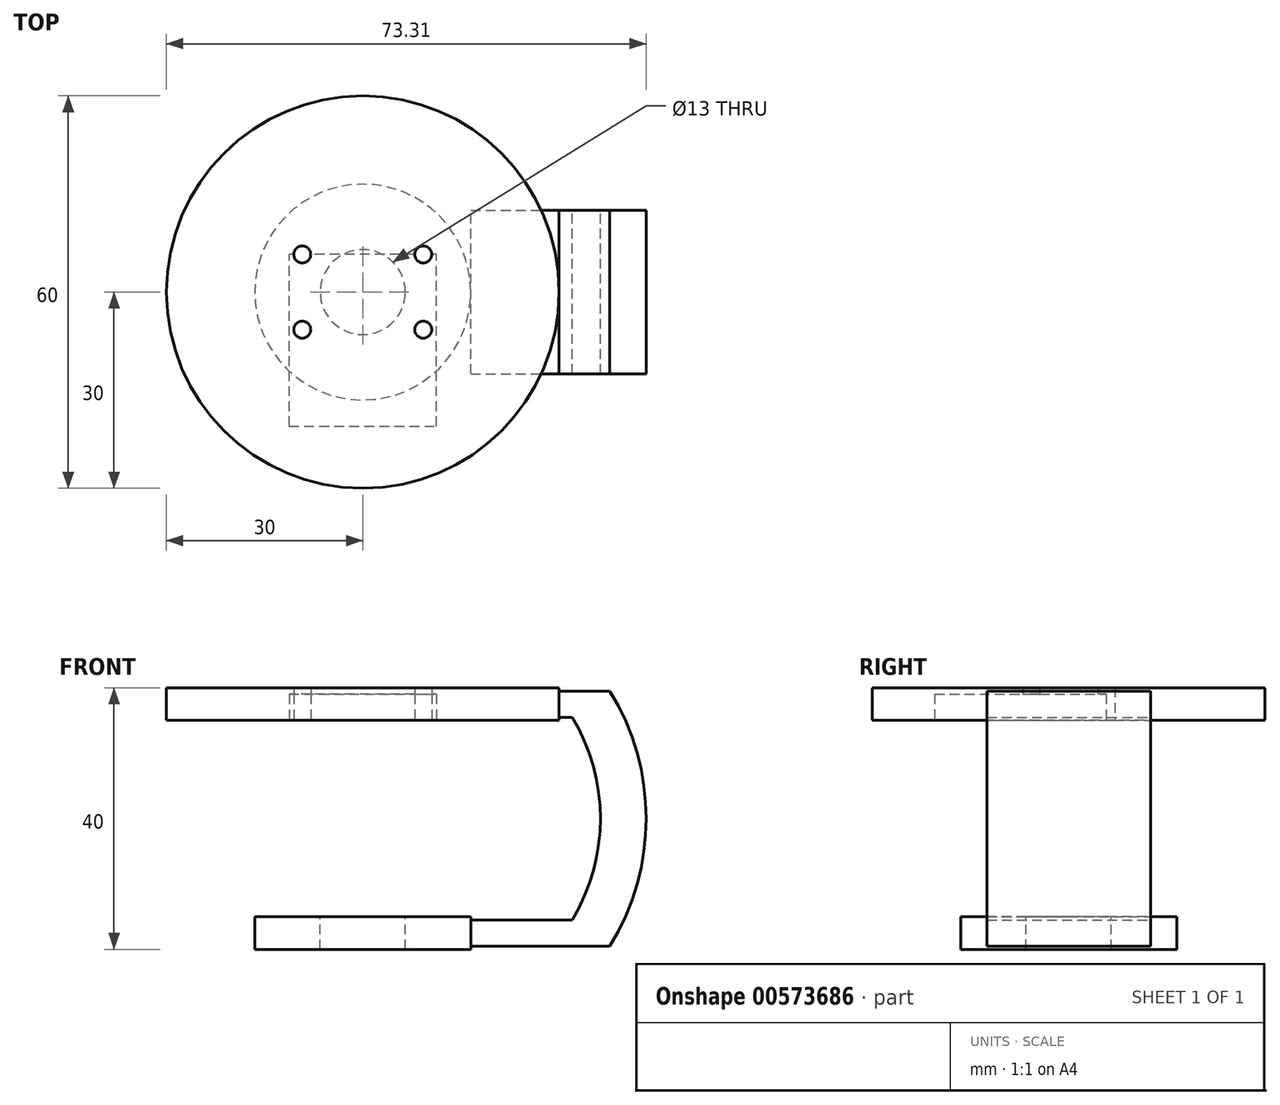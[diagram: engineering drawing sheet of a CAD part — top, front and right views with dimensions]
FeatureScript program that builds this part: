
annotation { "Feature Type Name" : "Feature", "Feature Type Description" : "" }
export const myFeature = defineFeature(function(context is Context, id is Id, definition is map)
    precondition{}
    {
        {
            var Q0;
            Q0=qCreatedBy(makeId("Front.planeOp"),FACE);
            var sketch = newSketch(context, id + "F0", { "sketchPlane" : qUnion([Q0])});
            skLineSegment(sketch, "E0.bottom", {"start": v(16.5, 2.5) * mm, "end": v(-16.5, 2.5) * mm});
            skLineSegment(sketch, "E0.top", {"start": v(16.5, -2.5) * mm, "end": v(-16.5, -2.5) * mm});
            skLineSegment(sketch, "E0.left", {"start": v(16.5, 2.5) * mm, "end": v(16.5, -2.5) * mm});
            skLineSegment(sketch, "E0.right", {"start": v(-16.5, 2.5) * mm, "end": v(-16.5, -2.5) * mm});
            skPoint(sketch, "E0.middle", {"position": v(0, 0) * mm});
            skLineSegment(sketch, "E1", {"start": v(0, 2.5) * mm, "end": v(0, -2.5) * mm});
            skLineSegment(sketch, "E2.bottom", {"start": v(0, -2) * mm, "end": v(32, -2) * mm});
            skLineSegment(sketch, "E2.top", {"start": v(0, 2) * mm, "end": v(32, 2) * mm});
            skLineSegment(sketch, "E2.left", {"start": v(0, -2) * mm, "end": v(0, 2) * mm});
            skLineSegment(sketch, "E2.right", {"start": v(32, -2) * mm, "end": v(32, 2) * mm});
            skLineSegment(sketch, "E3.bottom", {"start": v(30, 37.5) * mm, "end": v(-30, 37.5) * mm});
            skLineSegment(sketch, "E3.top", {"start": v(30, 32.5) * mm, "end": v(-30, 32.5) * mm});
            skLineSegment(sketch, "E3.left", {"start": v(30, 37.5) * mm, "end": v(30, 32.5) * mm});
            skLineSegment(sketch, "E3.right", {"start": v(-30, 37.5) * mm, "end": v(-30, 32.5) * mm});
            skPoint(sketch, "E3.middle", {"position": v(0, 35) * mm});
            skLineSegment(sketch, "E4", {"start": v(0, 37.5) * mm, "end": v(0, 32.5) * mm});
            skLineSegment(sketch, "E5.bottom", {"start": v(0, 33) * mm, "end": v(32, 33) * mm});
            skLineSegment(sketch, "E5.top", {"start": v(0, 37) * mm, "end": v(32, 37) * mm});
            skLineSegment(sketch, "E5.left", {"start": v(0, 33) * mm, "end": v(0, 37) * mm});
            skLineSegment(sketch, "E5.right", {"start": v(32, 33) * mm, "end": v(32, 37) * mm});
            skArc(sketch, "E6", {"start": v(32, 2) * mm, "mid": v(36.31, 17.5) * mm, "end": v(32, 33) * mm});
            skArc(sketch, "E7.0", {"start": v(37.76, -2) * mm, "mid": v(43.31, 17.5) * mm, "end": v(37.76, 37) * mm});
            skLineSegment(sketch, "E8", {"start": v(32, 37) * mm, "end": v(37.76, 37) * mm});
            skLineSegment(sketch, "E9", {"start": v(32, -2) * mm, "end": v(37.76, -2) * mm});
            skSolve(sketch);
        }
        {
            var Q0;
            {var subQ0=sQuery(id+"F0.wireOp",EDGE,"E0.right");Q0=makeQuery(id+"F0.imprint","IMPRINT",FACE,{"disambiguationData":[TD([[makeQuery(id+"F0.imprint","IMPRINT",EDGE,{"derivedFrom":subQ0}),1.0]])]});}
            var Q1;
            Q1=sQuery(id+"F0.wireOp",EDGE,"E1");
            revolve(context, id + "F1", {"entities" : qUnion([Q0]), "axis" : qUnion([Q1]), "revolveType" : RevolveType.FULL});
        }
        {
            var Q0;
            {var subQ0=sQuery(id+"F0.wireOp",EDGE,"E3.right");Q0=makeQuery(id+"F0.imprint","IMPRINT",FACE,{"disambiguationData":[TD([[makeQuery(id+"F0.imprint","IMPRINT",EDGE,{"derivedFrom":subQ0}),1.0]])]});}
            var Q1;
            Q1=sQuery(id+"F0.wireOp",EDGE,"E4");
            revolve(context, id + "F2", {"entities" : qUnion([Q0]), "axis" : qUnion([Q1]), "revolveType" : RevolveType.FULL});
        }
        {
            var Q0;
            {var subQ5=sQuery(id+"F0.wireOp",EDGE,"E2.right");Q0=makeQuery(id+"F0.imprint","IMPRINT",FACE,{"disambiguationData":[TD([[makeQuery(id+"F0.imprint","IMPRINT",EDGE,{"derivedFrom":subQ5}),1.0]])]});}
            var Q1;
            Q1=makeQuery(id+"F0.imprint","IMPRINT",FACE,{"disambiguationData":[TD([[makeQuery(id+"F0.imprint","IMPRINT",EDGE,{"derivedFrom":sQuery(id+"F0.wireOp",EDGE,"E2.right")}),-1.0]])]});
            var Q2;
            {var subQ5=sQuery(id+"F0.wireOp",EDGE,"E5.right");Q2=makeQuery(id+"F0.imprint","IMPRINT",FACE,{"disambiguationData":[TD([[makeQuery(id+"F0.imprint","IMPRINT",EDGE,{"derivedFrom":subQ5}),1.0]])]});}
            var Q3;
            {var subQ5=sQuery(id+"F0.wireOp",EDGE,"E2.left");Q3=makeQuery(id+"F0.imprint","IMPRINT",FACE,{"disambiguationData":[TD([[makeQuery(id+"F0.imprint","IMPRINT",EDGE,{"derivedFrom":subQ5}),-1.0]])]});}
            var Q4;
            {var subQ5=sQuery(id+"F0.wireOp",EDGE,"E5.left");Q4=makeQuery(id+"F0.imprint","IMPRINT",FACE,{"disambiguationData":[TD([[makeQuery(id+"F0.imprint","IMPRINT",EDGE,{"derivedFrom":subQ5}),-1.0]])]});}
            extrude(context, id + "F3", {"entities" : qUnion([Q0, Q1, Q2, Q3, Q4]), "endBound" : BoundingType.SYMMETRIC, "depth" : 25 * mm, "offsetDistance" : 25 * mm});
        }
        {
            var Q0;
            Q0=makeQuery(id+"F1.opRevolve","SWEPT_FACE",FACE,{"disambiguationData":[OSD([sQuery(id+"F0.wireOp",EDGE,"E0.bottom")])]});
            var sketch = newSketch(context, id + "F4", { "sketchPlane" : qUnion([Q0])});
            skCircle(sketch, "E10", {"center": v(0, 0) * mm, "radius": 12 * mm});
            skPoint(sketch, "E11", {"position": v(0, 12) * mm});
            skSolve(sketch);
        }
        {
            var Q0;
            Q0=sQuery(id+"F4.wireOp",VERTEX,"E11");
            var Q1;
            Q1=makeQuery(id+"F2.opRevolve","SWEPT_BODY",BODY,{"disambiguationData":[OSD([sQuery(id+"F0.wireOp",EDGE,"E3.bottom"),sQuery(id+"F0.wireOp",EDGE,"E3.top"),sQuery(id+"F0.wireOp",EDGE,"E3.right"),sQuery(id+"F0.wireOp",EDGE,"E4"),sQuery(id+"F0.wireOp",EDGE,"E5.left")])]});
            hole(context, id + "F5", {"style" : HoleStyle.SIMPLE, "endStyle" : HoleEndStyle.THROUGH, "standardTappedOrClearance" : lookupTablePath({ "standard" : "ISO", "fit" : "Normal", "size" : "M3", "type" : "Clearance" }), "standardBlindInLast" : lookupTablePath({ "fit" : "Standard", "standard" : "ISO", "size" : "M3", "type" : "Clearance" }), "holeDiameter" : 3.3 * mm, "isTappedThrough" : true, "tappedDepth" : 12.7 * mm, "tapClearance" : 3, "locations" : qUnion([Q0]), "scope" : qUnion([Q1])});
        }
        {
            var Q0;
            Q0=makeQuery(id+"F1.opRevolve","SWEPT_FACE",FACE,{"disambiguationData":[OSD([sQuery(id+"F0.wireOp",EDGE,"E0.bottom")])]});
            var sketch = newSketch(context, id + "F6", { "sketchPlane" : qUnion([Q0])});
            skCircle(sketch, "E12", {"center": v(0, 0) * mm, "radius": 6.5 * mm});
            skSolve(sketch);
        }
        {
            var Q0;
            Q0=makeQuery(id+"F6.imprint","IMPRINT",FACE,{"disambiguationData":[TD([[makeQuery(id+"F6.imprint","IMPRINT",EDGE,{"derivedFrom":sQuery(id+"F6.wireOp",EDGE,"E12")}),1.0]])]});
            extrude(context, id + "F7", {"entities" : qUnion([Q0]), "operationType" : NewBodyOperationType.REMOVE, "oppositeDirection" : true, "depth" : 6 * mm, "offsetDistance" : 25 * mm});
        }
        {
            var Q0;
            Q0=makeQuery(id+"F2.opRevolve","SWEPT_FACE",FACE,{"disambiguationData":[OSD([sQuery(id+"F0.wireOp",EDGE,"E3.top")])]});
            var sketch = newSketch(context, id + "F8", { "sketchPlane" : qUnion([Q0])});
            skLineSegment(sketch, "E13.bottom", {"start": v(11.25, 5.75) * mm, "end": v(-11.25, 5.75) * mm});
            skLineSegment(sketch, "E13.top", {"start": v(11.25, -5.75) * mm, "end": v(-11.25, -5.75) * mm});
            skLineSegment(sketch, "E13.left", {"start": v(11.25, 5.75) * mm, "end": v(11.25, -5.75) * mm});
            skLineSegment(sketch, "E13.right", {"start": v(-11.25, 5.75) * mm, "end": v(-11.25, -5.75) * mm});
            skPoint(sketch, "E13.middle", {"position": v(0, 0) * mm});
            skLineSegment(sketch, "E14.bottom", {"start": v(-11.25, -5.75) * mm, "end": v(10.8, -5.75) * mm});
            skLineSegment(sketch, "E14.top", {"start": v(-11.25, 20.5) * mm, "end": v(11.25, 20.5) * mm});
            skLineSegment(sketch, "E14.left", {"start": v(-11.25, -8) * mm, "end": v(-11.25, 20.5) * mm});
            skLineSegment(sketch, "E14.right", {"start": v(11.25, -8) * mm, "end": v(11.25, 20.5) * mm});
            skLineSegment(sketch, "E15", {"start": v(-11.25, -8) * mm, "end": v(11.25, -8) * mm});
            skPoint(sketch, "E16", {"position": v(-9.25, -5.75) * mm});
            skPoint(sketch, "E17", {"position": v(9.25, -5.75) * mm});
            skPoint(sketch, "E18", {"position": v(9.25, 5.75) * mm});
            skPoint(sketch, "E19", {"position": v(-9.25, 5.75) * mm});
            skSolve(sketch);
        }
        {
            var Q0;
            Q0=sQuery(id+"F8.wireOp",VERTEX,"E16");
            var Q1;
            Q1=sQuery(id+"F8.wireOp",VERTEX,"E19");
            var Q2;
            Q2=sQuery(id+"F8.wireOp",VERTEX,"E18");
            var Q3;
            Q3=sQuery(id+"F8.wireOp",VERTEX,"E17");
            var Q4;
            Q4=makeQuery(id+"F2.opRevolve","SWEPT_BODY",BODY,{"disambiguationData":[OSD([sQuery(id+"F0.wireOp",EDGE,"E3.bottom"),sQuery(id+"F0.wireOp",EDGE,"E3.top"),sQuery(id+"F0.wireOp",EDGE,"E3.right"),sQuery(id+"F0.wireOp",EDGE,"E4"),sQuery(id+"F0.wireOp",EDGE,"E5.left")])]});
            hole(context, id + "F9", {"style" : HoleStyle.SIMPLE, "endStyle" : HoleEndStyle.THROUGH, "holeDiameter" : 2.6 * mm, "isTappedThrough" : true, "tappedDepth" : 12.7 * mm, "tapClearance" : 3, "locations" : qUnion([Q0, Q1, Q2, Q3]), "scope" : qUnion([Q4])});
        }
        {
            var Q0;
            {var subQ0=sQuery(id+"F8.wireOp",EDGE,"E14.bottom");Q0=makeQuery(id+"F8.imprint","IMPRINT",FACE,{"disambiguationData":[TD([[makeQuery(id+"F8.imprint","IMPRINT",EDGE,{"derivedFrom":subQ0}),-1.0]])]});}
            var Q1;
            {var subQ0=sQuery(id+"F8.wireOp",EDGE,"E13.bottom");Q1=makeQuery(id+"F8.imprint","IMPRINT",FACE,{"disambiguationData":[TD([[makeQuery(id+"F8.imprint","IMPRINT",EDGE,{"derivedFrom":subQ0}),1.0]])]});}
            var Q2;
            {var subQ0=sQuery(id+"F8.wireOp",EDGE,"E13.bottom");Q2=makeQuery(id+"F8.imprint","IMPRINT",FACE,{"disambiguationData":[TD([[makeQuery(id+"F8.imprint","IMPRINT",EDGE,{"derivedFrom":subQ0}),-1.0]])]});}
            extrude(context, id + "F10", {"entities" : qUnion([Q0, Q1, Q2]), "operationType" : NewBodyOperationType.REMOVE, "oppositeDirection" : true, "depth" : 4 * mm, "offsetDistance" : 25 * mm});
        }
    });
